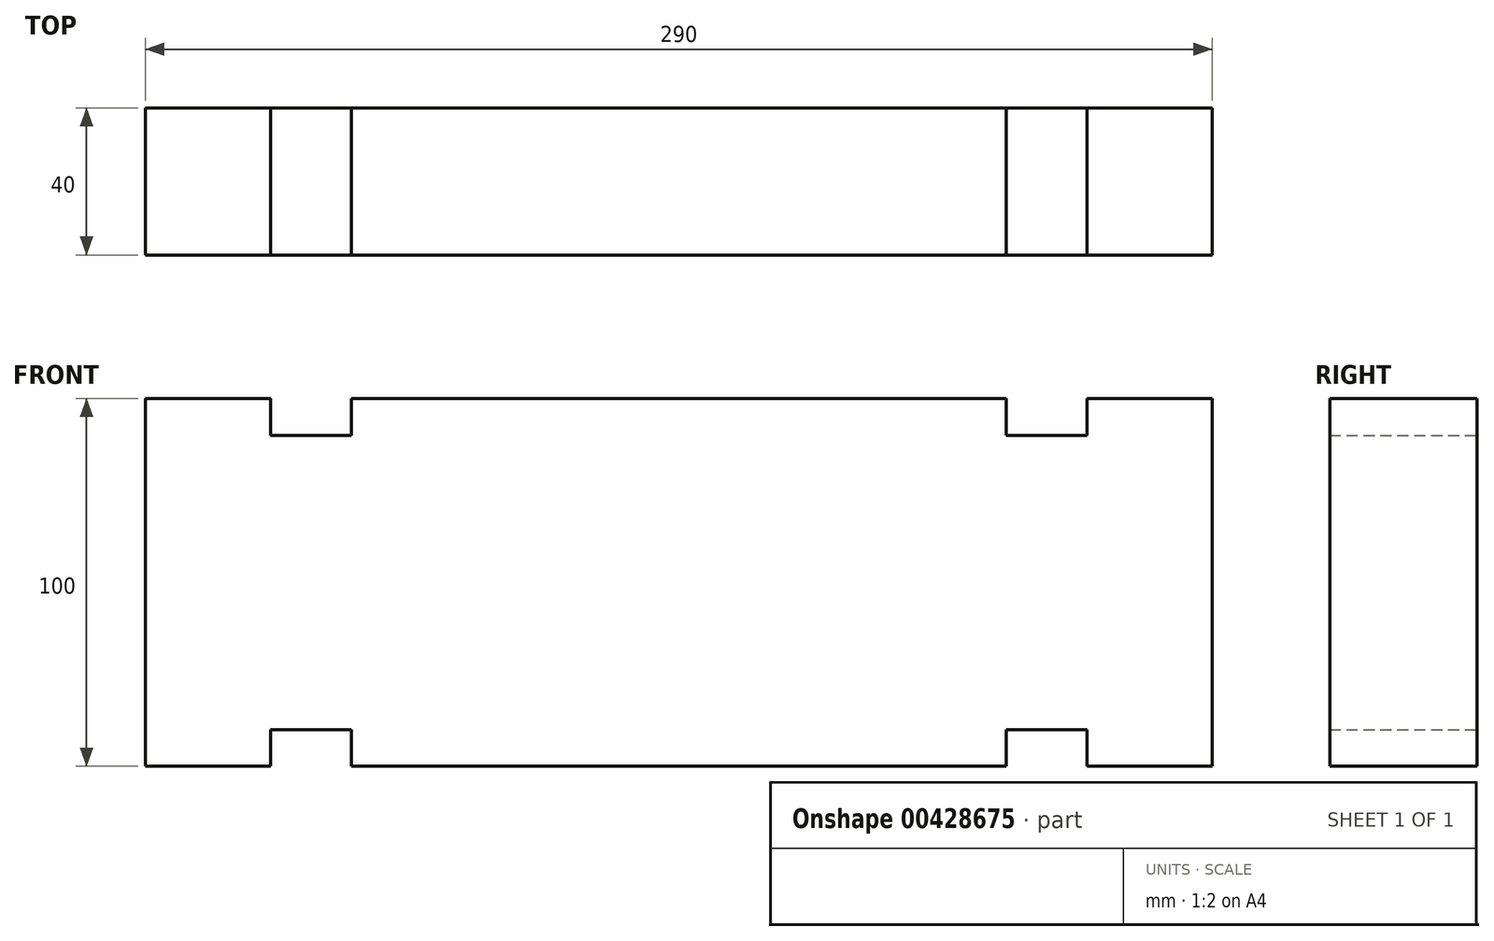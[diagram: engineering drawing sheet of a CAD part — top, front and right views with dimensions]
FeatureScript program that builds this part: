
annotation { "Feature Type Name" : "Feature", "Feature Type Description" : "" }
export const myFeature = defineFeature(function(context is Context, id is Id, definition is map)
    precondition{}
    {
        {
            var Q0;
            Q0=qCreatedBy(makeId("Front.planeOp"),FACE);
            var sketch = newSketch(context, id + "F0", { "sketchPlane" : qUnion([Q0])});
            skLineSegment(sketch, "E0.bottom", {"start": v(145, -50) * mm, "end": v(111, -50) * mm});
            skLineSegment(sketch, "E0.top", {"start": v(145, 50) * mm, "end": v(111, 50) * mm});
            skLineSegment(sketch, "E0.left", {"start": v(145, -50) * mm, "end": v(145, 50) * mm});
            skLineSegment(sketch, "E0.right", {"start": v(-145, -50) * mm, "end": v(-145, 50) * mm});
            skPoint(sketch, "E0.middle", {"position": v(0, 0) * mm});
            skLineSegment(sketch, "E1", {"start": v(0, 50) * mm, "end": v(89, 50) * mm});
            skLineSegment(sketch, "E2", {"start": v(0, 50) * mm, "end": v(-89, 50) * mm});
            skLineSegment(sketch, "E3", {"start": v(89, 50) * mm, "end": v(89, 40) * mm});
            skLineSegment(sketch, "E4", {"start": v(111, -50) * mm, "end": v(111, -40) * mm});
            skLineSegment(sketch, "E5", {"start": v(111, -40) * mm, "end": v(89, -40) * mm});
            skLineSegment(sketch, "E6", {"start": v(89, 40) * mm, "end": v(111, 40) * mm});
            skLineSegment(sketch, "E7", {"start": v(111, 40) * mm, "end": v(111, 50) * mm});
            skLineSegment(sketch, "E8", {"start": v(-138.92, 50) * mm, "end": v(-111, 50) * mm});
            skLineSegment(sketch, "E9", {"start": v(-134.43, 50) * mm, "end": v(-111, 50) * mm});
            skLineSegment(sketch, "E10", {"start": v(-128.9, 50) * mm, "end": v(-111, 50) * mm});
            skLineSegment(sketch, "E11.trimOffspring", {"start": v(89, -40) * mm, "end": v(89, -50) * mm});
            skLineSegment(sketch, "E12.trimOffspring", {"start": v(89, 50) * mm, "end": v(-89, 50) * mm});
            skLineSegment(sketch, "E13.trimOffspring", {"start": v(89, -50) * mm, "end": v(-89, -50) * mm});
            skLineSegment(sketch, "E14", {"start": v(0, -50) * mm, "end": v(-89, -50) * mm});
            skLineSegment(sketch, "E15", {"start": v(-111, -50) * mm, "end": v(-111, -40) * mm});
            skLineSegment(sketch, "E16", {"start": v(-89, 50) * mm, "end": v(-89, 40) * mm});
            skLineSegment(sketch, "E17", {"start": v(-111, -40) * mm, "end": v(-89, -40) * mm});
            skLineSegment(sketch, "E18", {"start": v(-111, 40) * mm, "end": v(-89, 40) * mm});
            skLineSegment(sketch, "E19.trimOffspring", {"start": v(-89, -40) * mm, "end": v(-89, -50) * mm});
            skLineSegment(sketch, "E20.trimOffspring", {"start": v(-111, 40) * mm, "end": v(-111, 50) * mm});
            skLineSegment(sketch, "E21.trimOffspring", {"start": v(-111, 50) * mm, "end": v(-145, 50) * mm});
            skLineSegment(sketch, "E22.trimOffspring", {"start": v(-111, -50) * mm, "end": v(-145, -50) * mm});
            skSolve(sketch);
        }
        {
            var Q0;
            Q0 = qSketchRegion(id + "F0", true);
            extrude(context, id + "F1", {"entities" : qUnion([Q0]), "depth" : 40 * mm});
        }
    });
